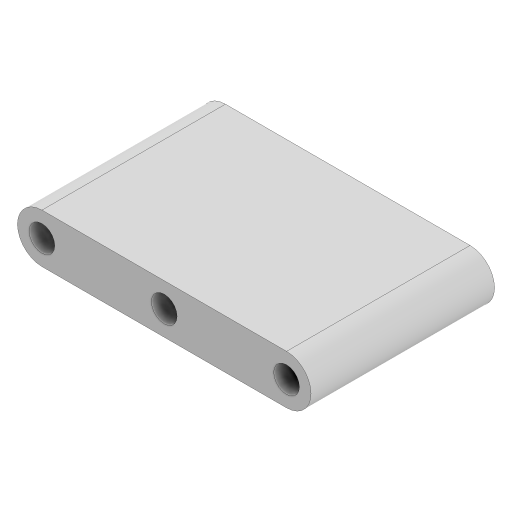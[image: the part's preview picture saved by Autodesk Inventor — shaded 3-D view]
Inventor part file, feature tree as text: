
AUTODESK INVENTOR PART (.ipt)
format: ipt  version: 2023 (Build 270158000, 158)  size: 104,960 bytes
history: native  units: mm
features: extrude x1, sketch x1
ambient origin geometry x8: Origin, YZ Plane, XZ Plane, XY Plane, X Axis, Y Axis, Z Axis, Center Point
bodies: Solid1 (feature_tree)
feature tree (2):
  extrude  "Extrusion1"  Depth=30.0mm
  sketch  "Sketch1"  dims[d0=4.2mm d1=4.2mm d2=4.2mm d3=20.0mm d4=20.0mm d5=0.0mm d6=8.0mm d7=30.0mm d8=0.0mm]
